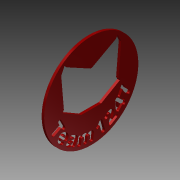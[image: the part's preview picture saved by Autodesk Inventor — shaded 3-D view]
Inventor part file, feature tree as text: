
AUTODESK INVENTOR PART (.ipt)
format: ipt  version: 2014 (Build 180170000, 170)  size: 1,392,640 bytes
history: native  units: in
note: dims shown in document units (in); Inventor stores cm internally (conversion verified against a paired STEP export)
features: sketch x23, extrude x16, plane x9, projected_geometry x8, loft x4, other x4, fillet x2, mirror x1, chamfer x1
ambient origin geometry x8: Origin, YZ Plane, XZ Plane, XY Plane, X Axis, Y Axis, Z Axis, Center Point
bodies: Solid1 (feature_tree)
feature tree (68):
  sketch  "Sketch1"  dims[d0=0.7559in d1=0.7559in]
  plane  "Work Plane1"
  loft  "Main Body"
  extrude  "Right Eye"  Depth=0.2in
  plane  "Work Plane4"
  loft  "Main Nose"
  plane  "Work Plane5"
  loft  "Back of Head"
  loft  "Main Ear - Right"
  extrude  "Inside of Ear - Right"  TaperAngle=0.0deg  [1 undecoded]
  plane  "Work Plane6"
  extrude  "Top and TopSide Rivets - Long"  Depth=1.0in
  extrude  "Top Most Rivet -  Cut Down"  Depth=1.0651in
  extrude  "Top Lower Rivet - Cut Down"  Depth=0.962in
  plane  "Work Plane7"
  extrude  "Side Rivets"  Depth=0.075in
  plane  "Work Plane8"
  other  "Work Axis1"
  plane  "Work Plane9"
  extrude  "Ear Shaping - Right"  Depth=0.06in
  mirror  "Eye, Ear and Rivet Mirro"
  extrude  "Fill Back (Make it a flat Print)"  Depth=0.05in
  plane  "Work Plane10"
  extrude  "Fill Back 2"  Depth=0.0625in
  plane  "Work Plane11"
  extrude  "Cut Back 1 (Adjust Angle)"  Depth=0.075in
  extrude  "Cut Back 2"  TaperAngle=0.0deg  [1 undecoded]
  extrude  "Round Back"  Depth=0.2in
  extrude  "Lip"  TaperAngle=0.0deg  [1 undecoded]
  other  "Team Text"
  extrude  "Remove Area for Ears"  Depth=0.01in
  extrude  "Remove Area for Nose"  Depth=0.0344in
  chamfer  "Chamfer Eyes"  Distance=0.05in
  fillet  "Fill Bridge of Nose"  Radius=0.05in
  fillet  "Fillet3"  Radius=0.05in
  extrude  "Extrusion19"  Depth=0.05in
  sketch  "Sketch2"  dims[d2=0.9963in d3=0.2in]
  sketch  "Sketch3"  dims[d4=0.5in d6=0.08in]
  sketch  "Sketch4"  dims[d7=0.55in d8=150.0deg]
  other  "Edges1"
  sketch  "Sketch5"  dims[d9=150.0deg d14=0.33in]
  projected_geometry  "Projected Loop1"
  other  "Edges2"
  sketch  "Sketch6"  dims[d15=0.66in d18=0.0in d19=90.0deg]
  sketch  "Sketch7"  dims[d20=0.0in d21=90.0deg d22=1.0in]
  sketch  "Sketch8"  dims[d26=1.0651in d28=1.0651in]
  sketch  "Sketch9"  dims[d29=0.0in d30=0.962in]
  sketch  "Sketch10"  dims[d31=0.962in d32=0.075in]
  sketch  "Sketch11"  dims[d33=0.15in d34=0.06in]
  sketch  "Sketch12"  dims[d35=0.1in d36=0.05in]
  sketch  "Sketch13"  dims[d37=0.45in d38=0.0in d39=0.0625in]
  projected_geometry  "Projected Loop2"
  projected_geometry  "Projected Loop3"
  sketch  "Sketch14"  dims[d40=0.01in d41=0.075in]
  projected_geometry  "Projected Loop4"
  sketch  "Sketch15"  dims[d42=0.01in d43=0.0in d44=90.0deg]
  sketch  "Sketch16"  dims[d45=0.0in d46=90.0deg d47=0.2in]
  sketch  "Sketch17"  dims[d48=0.07in d49=0.0in d50=90.0deg]
  sketch  "Sketch18"  dims[d51=0.0in d52=90.0deg d53=0.01in]
  sketch  "Sketch19"  dims[d54=0.01in d55=0.0344in]
  sketch  "Sketch20"  dims[d56=150.0deg]
  sketch  "Sketch23"  dims[d57=60.0deg]
  projected_geometry  "Projected Loop6"
  sketch  "Sketch24"  dims[d58=150.0deg]
  sketch  "Sketch26"  dims[d59=0.7in d60=0.05in d61=0.05in d62=0.05in d63=0.05in d64=0.05in d65=0.01in d66=0.0in d67=90.0deg d68=0.0in d69=90.0deg d70=0.1in d71=0.4in d72=0.15in d73=0.05in d74=0.0in d75=0.02in d77=0.15in d78=0.02in d79=0.1in d80=0.1in d81=0.1in d82=0.02in d83=0.15in d84=0.05in d85=0.0in d86=0.045in d87=0.0in d88=0.025in d89=0.0in d90=0.02in d91=0.02in d92=0.005in d93=0.0in d94=90.0deg d95=0.4466in d96=1.0in d97=0.0in d98=1.0in d99=0.0in d100=0.6528in d101=0.0in d102=0.0in d103=1.0in d104=0.0in d106=90.0deg d107=1.0in d108=0.0in d109=1.65in d110=0.1in d111=0.075in d112=0.0in d113=0.1in d114=0.075in d115=0.0in d116=0.05in d117=0.0in d123=0.1in d124=0.0in d125=0.05in d126=0.0in d130=0.02in d131=0.125in d132=45.0deg d133=0.02in d137=0.02in d138=0.0375in d139=0.0in]
  projected_geometry  "Projected Loop10"
  projected_geometry  "Projected Loop11"
  projected_geometry  "Projected Loop12"
note: 3 required parameter values undecoded (feature->parameter linkage not recoverable at this tier; creation-order binding heuristic only, values carry confidence <= 0.55)
